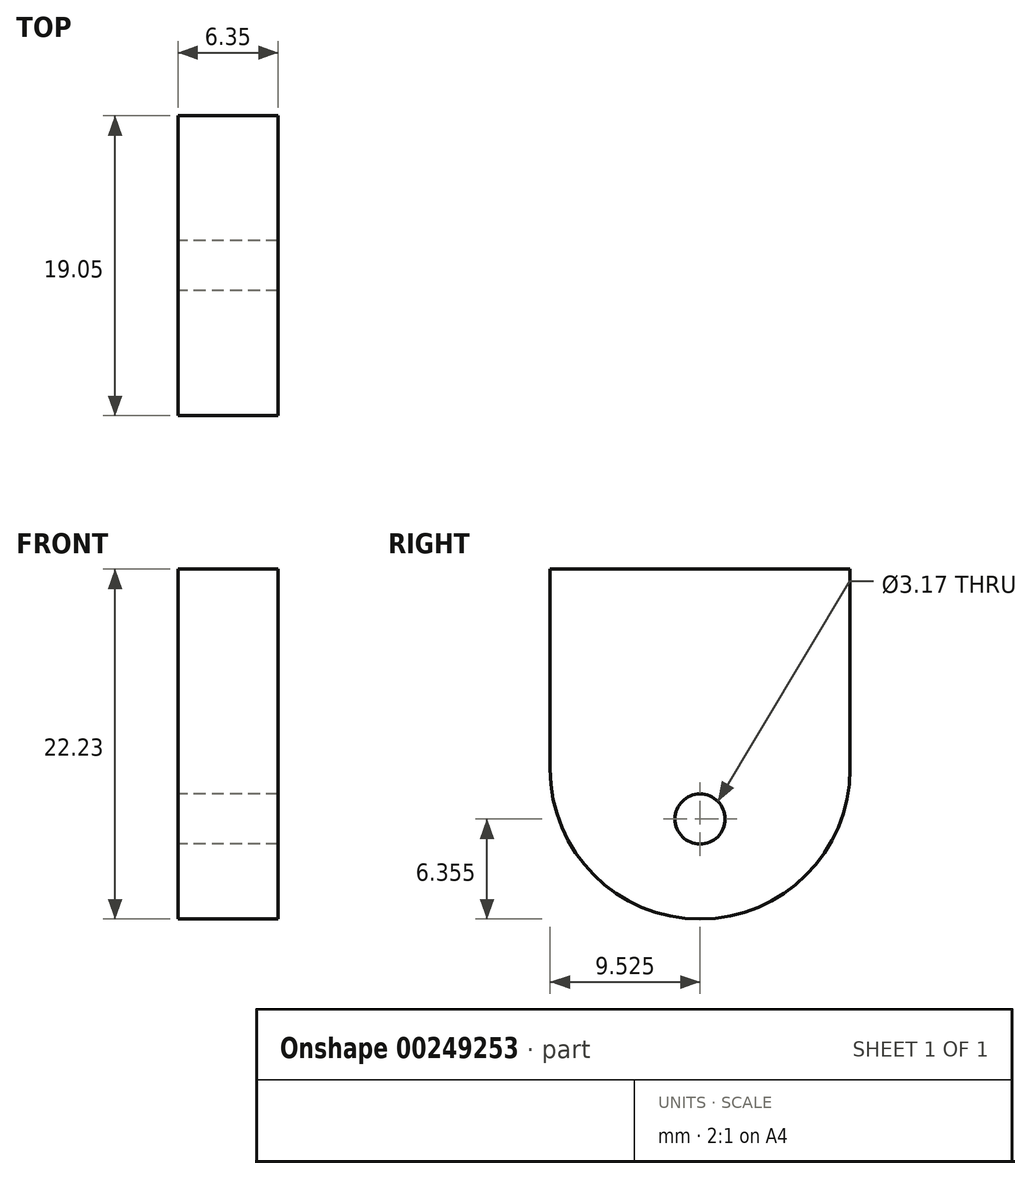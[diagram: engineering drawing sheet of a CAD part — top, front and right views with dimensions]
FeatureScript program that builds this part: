
annotation { "Feature Type Name" : "Feature", "Feature Type Description" : "" }
export const myFeature = defineFeature(function(context is Context, id is Id, definition is map)
    precondition{}
    {
        {
            var Q0;
            Q0=qCreatedBy(makeId("Right.planeOp"),FACE);
            var sketch = newSketch(context, id + "F0", { "sketchPlane" : qUnion([Q0])});
            skLineSegment(sketch, "E0", {"start": v(0, 0) * mm, "end": v(0, 12.7) * mm});
            skLineSegment(sketch, "E1", {"start": v(0, 12.7) * mm, "end": v(19.05, 12.7) * mm});
            skLineSegment(sketch, "E2", {"start": v(19.05, 12.7) * mm, "end": v(19.05, 0) * mm});
            skArc(sketch, "E3", {"start": v(0, 0) * mm, "mid": v(9.52, -9.53) * mm, "end": v(19.05, 0) * mm});
            skCircle(sketch, "E4", {"center": v(9.53, -3.18) * mm, "radius": 1.59 * mm});
            skSolve(sketch);
        }
        {
            var Q0;
            Q0=makeQuery(id+"F0.imprint","IMPRINT",FACE,{"disambiguationData":[TD([[makeQuery(id+"F0.imprint","IMPRINT",EDGE,{"derivedFrom":sQuery(id+"F0.wireOp",EDGE,"E0")}),-1.0]])]});
            extrude(context, id + "F1", {"entities" : qUnion([Q0]), "depth" : 6.35 * mm});
        }
    });
